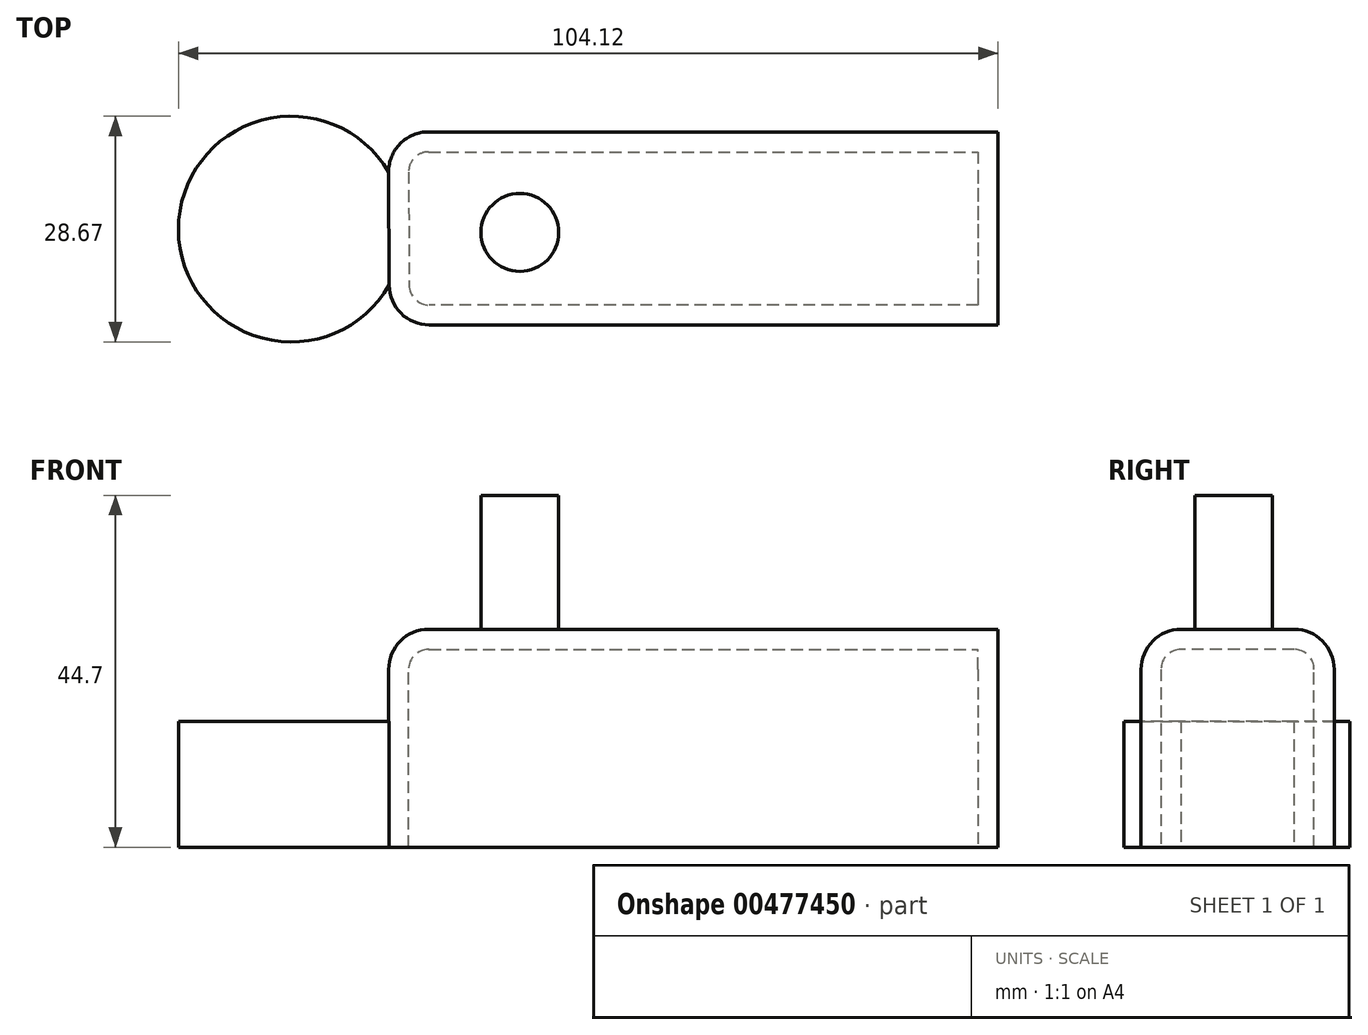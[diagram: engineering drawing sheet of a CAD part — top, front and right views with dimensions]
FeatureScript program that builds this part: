
annotation { "Feature Type Name" : "Feature", "Feature Type Description" : "" }
export const myFeature = defineFeature(function(context is Context, id is Id, definition is map)
    precondition{}
    {
        {
            var Q0;
            Q0=qCreatedBy(makeId("Top.planeOp"),FACE);
            var sketch = newSketch(context, id + "F0", { "sketchPlane" : qUnion([Q0])});
            skLineSegment(sketch, "E0", {"start": v(0, 0) * mm, "end": v(-77.32, 0) * mm});
            skLineSegment(sketch, "E1", {"start": v(-77.45, 24.52) * mm, "end": v(0, 24.52) * mm});
            skLineSegment(sketch, "E2", {"start": v(-77.45, 24.52) * mm, "end": v(-77.32, 0) * mm});
            skLineSegment(sketch, "E3", {"start": v(0, 24.52) * mm, "end": v(0, 0) * mm});
            skSolve(sketch);
        }
        {
            var Q0;
            Q0 = qSketchRegion(id + "F0", true);
            extrude(context, id + "F1", {"entities" : qUnion([Q0]), "depth" : 27.7 * mm});
        }
        {
            var Q0;
            Q0=makeQuery(id+"F1.opExtrude","SWEPT_EDGE",EDGE,{"disambiguationData":[OSD([sQuery(id+"F0.wireOp",EDGE,"E1"),sQuery(id+"F0.wireOp",EDGE,"E2")])]});
            var Q1;
            Q1=makeQuery(id+"F1.opExtrude","CAP_EDGE",EDGE,{"disambiguationData":[OSD([sQuery(id+"F0.wireOp",EDGE,"E1")])],"isStart":false});
            var Q2;
            Q2=makeQuery(id+"F1.opExtrude","CAP_EDGE",EDGE,{"disambiguationData":[OSD([sQuery(id+"F0.wireOp",EDGE,"E2")])],"isStart":false});
            var Q3;
            Q3=makeQuery(id+"F1.opExtrude","CAP_EDGE",EDGE,{"disambiguationData":[OSD([sQuery(id+"F0.wireOp",EDGE,"E0")])],"isStart":false});
            var Q4;
            Q4=makeQuery(id+"F1.opExtrude","SWEPT_EDGE",EDGE,{"disambiguationData":[OSD([sQuery(id+"F0.wireOp",EDGE,"E0"),sQuery(id+"F0.wireOp",EDGE,"E2")])]});
            fillet(context, id + "F2", {"entities" : qUnion([Q0, Q1, Q2, Q3, Q4]), "radius" : 5.08 * mm, "tangentPropagation" : true, "allowEdgeOverflow" : false});
        }
        {
            var Q0;
            Q0=makeQuery(id+"F1.opExtrude","CAP_FACE",FACE,{"disambiguationData":[OSD([sQuery(id+"F0.wireOp",EDGE,"E0"),sQuery(id+"F0.wireOp",EDGE,"E1"),sQuery(id+"F0.wireOp",EDGE,"E2"),sQuery(id+"F0.wireOp",EDGE,"E3")])],"isStart":true});
            shell(context, id + "F3", {"entities" : qUnion([Q0]), "thickness" : 2.54 * mm});
        }
        {
            var Q0;
            Q0=makeQuery(id+"F1.opExtrude","CAP_FACE",FACE,{"disambiguationData":[OSD([sQuery(id+"F0.wireOp",EDGE,"E0"),sQuery(id+"F0.wireOp",EDGE,"E1"),sQuery(id+"F0.wireOp",EDGE,"E2"),sQuery(id+"F0.wireOp",EDGE,"E3")])],"isStart":false});
            var sketch = newSketch(context, id + "F4", { "sketchPlane" : qUnion([Q0])});
            skCircle(sketch, "E4", {"center": v(-60.76, 11.75) * mm, "radius": 4.94 * mm});
            skSolve(sketch);
        }
        {
            var Q0;
            Q0 = qSketchRegion(id + "F4", true);
            extrude(context, id + "F5", {"entities" : qUnion([Q0]), "operationType" : NewBodyOperationType.ADD, "depth" : 17.02 * mm});
        }
        {
            var Q0;
            Q0=makeQuery(id+"F1.opExtrude","CAP_FACE",FACE,{"disambiguationData":[OSD([sQuery(id+"F0.wireOp",EDGE,"E0"),sQuery(id+"F0.wireOp",EDGE,"E1"),sQuery(id+"F0.wireOp",EDGE,"E2"),sQuery(id+"F0.wireOp",EDGE,"E3")])],"isStart":true});
            var sketch = newSketch(context, id + "F6", { "sketchPlane" : qUnion([Q0])});
            skArc(sketch, "E5", {"start": v(-77.35, -5.05) * mm, "mid": v(-104.12, -12.1) * mm, "end": v(-77.42, -19.42) * mm});
            skSolve(sketch);
        }
        {
            var Q0;
            Q0=makeQuery(id+"F6.imprint","IMPRINT",FACE,{"disambiguationData":[TD([[makeQuery(id+"F6.imprint","IMPRINT",EDGE,{"derivedFrom":sQuery(id+"F6.wireOp",EDGE,"E5")}),1.0]])]});
            extrude(context, id + "F7", {"entities" : qUnion([Q0]), "operationType" : NewBodyOperationType.ADD, "oppositeDirection" : true, "depth" : 16 * mm});
        }
    });
